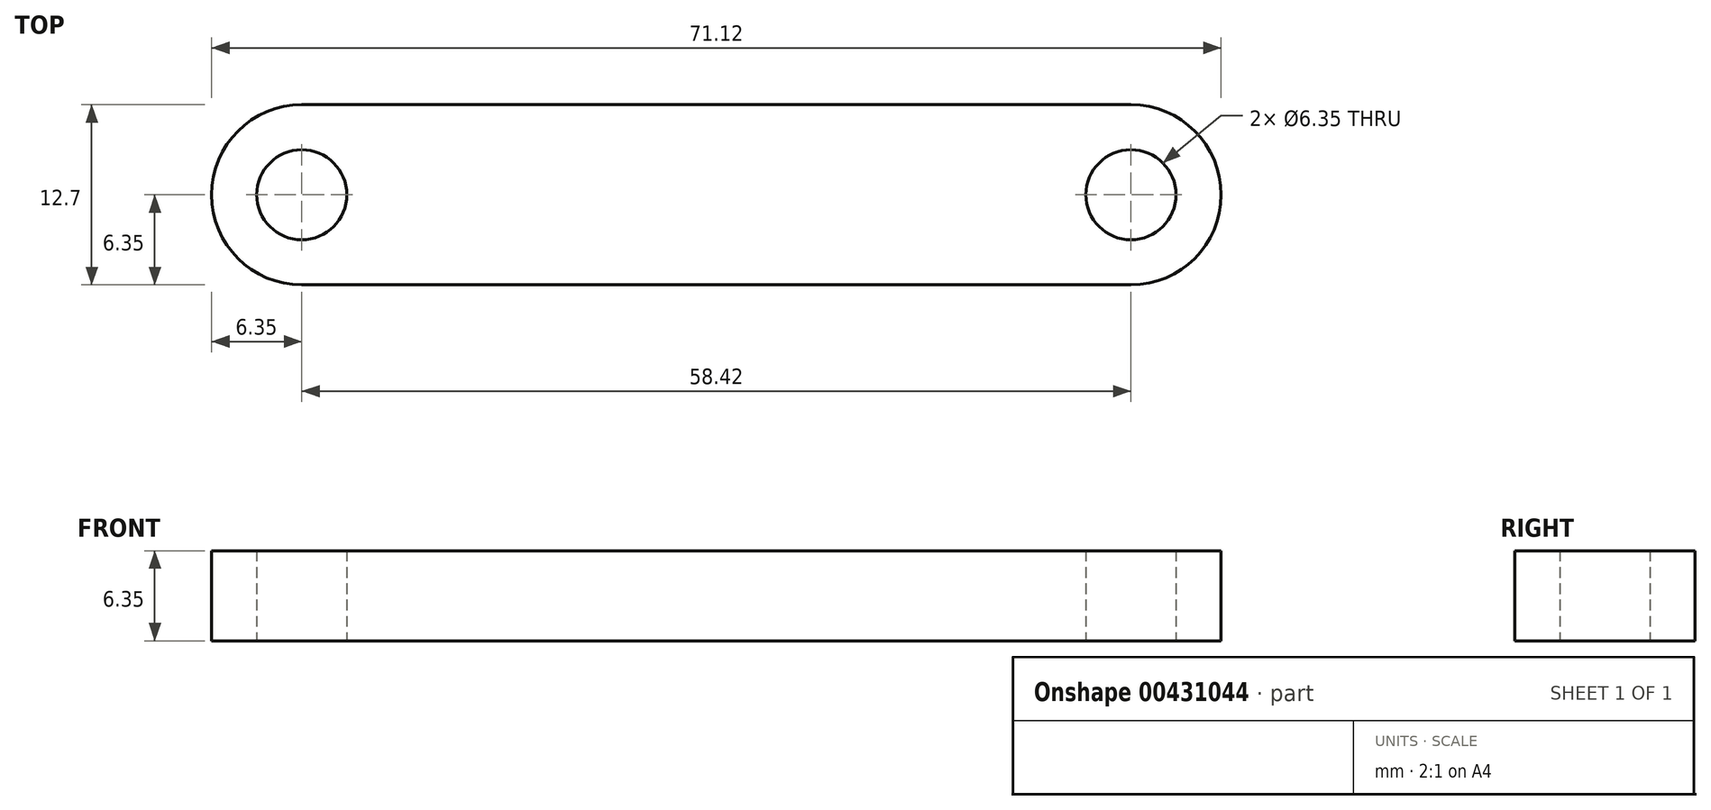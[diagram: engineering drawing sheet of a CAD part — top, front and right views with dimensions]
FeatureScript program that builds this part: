
annotation { "Feature Type Name" : "Feature", "Feature Type Description" : "" }
export const myFeature = defineFeature(function(context is Context, id is Id, definition is map)
    precondition{}
    {
        {
            var Q0;
            Q0=qCreatedBy(makeId("Top.planeOp"),FACE);
            var sketch = newSketch(context, id + "F0", { "sketchPlane" : qUnion([Q0])});
            skLineSegment(sketch, "E0", {"start": v(-29.21, 6.35) * mm, "end": v(29.21, 6.35) * mm});
            skLineSegment(sketch, "E1", {"start": v(-29.21, -6.35) * mm, "end": v(29.2, -6.35) * mm});
            skArc(sketch, "E2", {"start": v(-29.21, 6.35) * mm, "mid": v(-35.56, 0) * mm, "end": v(-29.21, -6.35) * mm});
            skArc(sketch, "E3", {"start": v(29.21, -6.35) * mm, "mid": v(35.56, 0) * mm, "end": v(29.21, 6.35) * mm});
            skPoint(sketch, "E4", {"position": v(0, 6.35) * mm});
            skCircle(sketch, "E5", {"center": v(-29.21, 0) * mm, "radius": 3.18 * mm});
            skCircle(sketch, "E6", {"center": v(29.21, 0) * mm, "radius": 3.18 * mm});
            skSolve(sketch);
        }
        {
            var Q0;
            Q0 = qSketchRegion(id + "F0", true);
            extrude(context, id + "F1", {"entities" : qUnion([Q0]), "depth" : 6.35 * mm});
        }
    });
